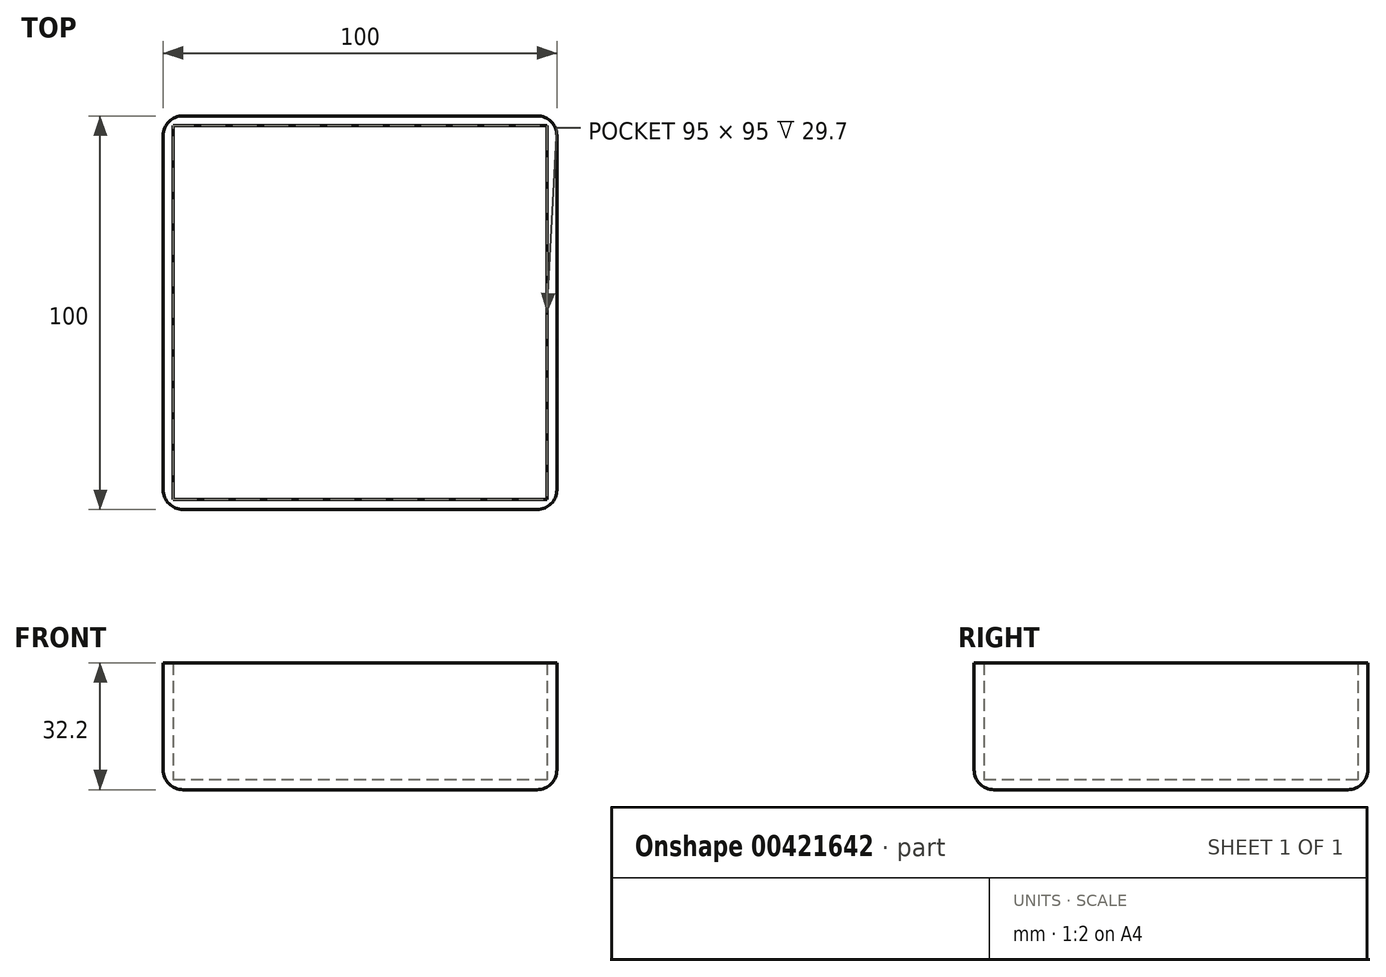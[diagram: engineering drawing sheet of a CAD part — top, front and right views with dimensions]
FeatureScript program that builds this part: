
annotation { "Feature Type Name" : "Feature", "Feature Type Description" : "" }
export const myFeature = defineFeature(function(context is Context, id is Id, definition is map)
    precondition{}
    {
        {
            var Q0;
            Q0=qCreatedBy(makeId("Top.planeOp"),FACE);
            var sketch = newSketch(context, id + "F0", { "sketchPlane" : qUnion([Q0])});
            skLineSegment(sketch, "E0.bottom", {"start": v(50, 50) * mm, "end": v(-50, 50) * mm});
            skLineSegment(sketch, "E0.top", {"start": v(50, -50) * mm, "end": v(-50, -50) * mm});
            skLineSegment(sketch, "E0.left", {"start": v(50, 50) * mm, "end": v(50, -50) * mm});
            skLineSegment(sketch, "E0.right", {"start": v(-50, 50) * mm, "end": v(-50, -50) * mm});
            skPoint(sketch, "E0.middle", {"position": v(0, 0) * mm});
            skSolve(sketch);
        }
        {
            var Q0;
            Q0 = qSketchRegion(id + "F0", true);
            extrude(context, id + "F1", {"entities" : qUnion([Q0]), "depth" : 32.2 * mm});
        }
        {
            var Q0;
            Q0=makeQuery(id+"F1.opExtrude","CAP_FACE",FACE,{"disambiguationData":[OSD([sQuery(id+"F0.wireOp",EDGE,"E0.bottom"),sQuery(id+"F0.wireOp",EDGE,"E0.top"),sQuery(id+"F0.wireOp",EDGE,"E0.left"),sQuery(id+"F0.wireOp",EDGE,"E0.right")])],"isStart":false});
            shell(context, id + "F2", {"entities" : qUnion([Q0]), "thickness" : 2.5 * mm});
        }
        {
            var Q0;
            Q0=makeQuery(id+"F1.opExtrude","CAP_EDGE",EDGE,{"disambiguationData":[OSD([sQuery(id+"F0.wireOp",EDGE,"E0.top")])],"isStart":true});
            var Q1;
            Q1=makeQuery(id+"F1.opExtrude","SWEPT_EDGE",EDGE,{"disambiguationData":[OSD([sQuery(id+"F0.wireOp",EDGE,"E0.top"),sQuery(id+"F0.wireOp",EDGE,"E0.right")])]});
            var Q2;
            Q2=makeQuery(id+"F1.opExtrude","SWEPT_EDGE",EDGE,{"disambiguationData":[OSD([sQuery(id+"F0.wireOp",EDGE,"E0.bottom"),sQuery(id+"F0.wireOp",EDGE,"E0.left")])]});
            var Q3;
            Q3=makeQuery(id+"F1.opExtrude","SWEPT_EDGE",EDGE,{"disambiguationData":[OSD([sQuery(id+"F0.wireOp",EDGE,"E0.top"),sQuery(id+"F0.wireOp",EDGE,"E0.left")])]});
            var Q4;
            Q4=makeQuery(id+"F1.opExtrude","CAP_EDGE",EDGE,{"disambiguationData":[OSD([sQuery(id+"F0.wireOp",EDGE,"E0.left")])],"isStart":true});
            var Q5;
            Q5=makeQuery(id+"F1.opExtrude","CAP_EDGE",EDGE,{"disambiguationData":[OSD([sQuery(id+"F0.wireOp",EDGE,"E0.bottom")])],"isStart":true});
            var Q6;
            Q6=makeQuery(id+"F1.opExtrude","SWEPT_EDGE",EDGE,{"disambiguationData":[OSD([sQuery(id+"F0.wireOp",EDGE,"E0.bottom"),sQuery(id+"F0.wireOp",EDGE,"E0.right")])]});
            var Q7;
            Q7=makeQuery(id+"F1.opExtrude","CAP_EDGE",EDGE,{"disambiguationData":[OSD([sQuery(id+"F0.wireOp",EDGE,"E0.right")])],"isStart":true});
            fillet(context, id + "F3", {"entities" : qUnion([Q0, Q1, Q2, Q3, Q4, Q5, Q6, Q7]), "radius" : 5 * mm, "tangentPropagation" : true, "allowEdgeOverflow" : false});
        }
    });
